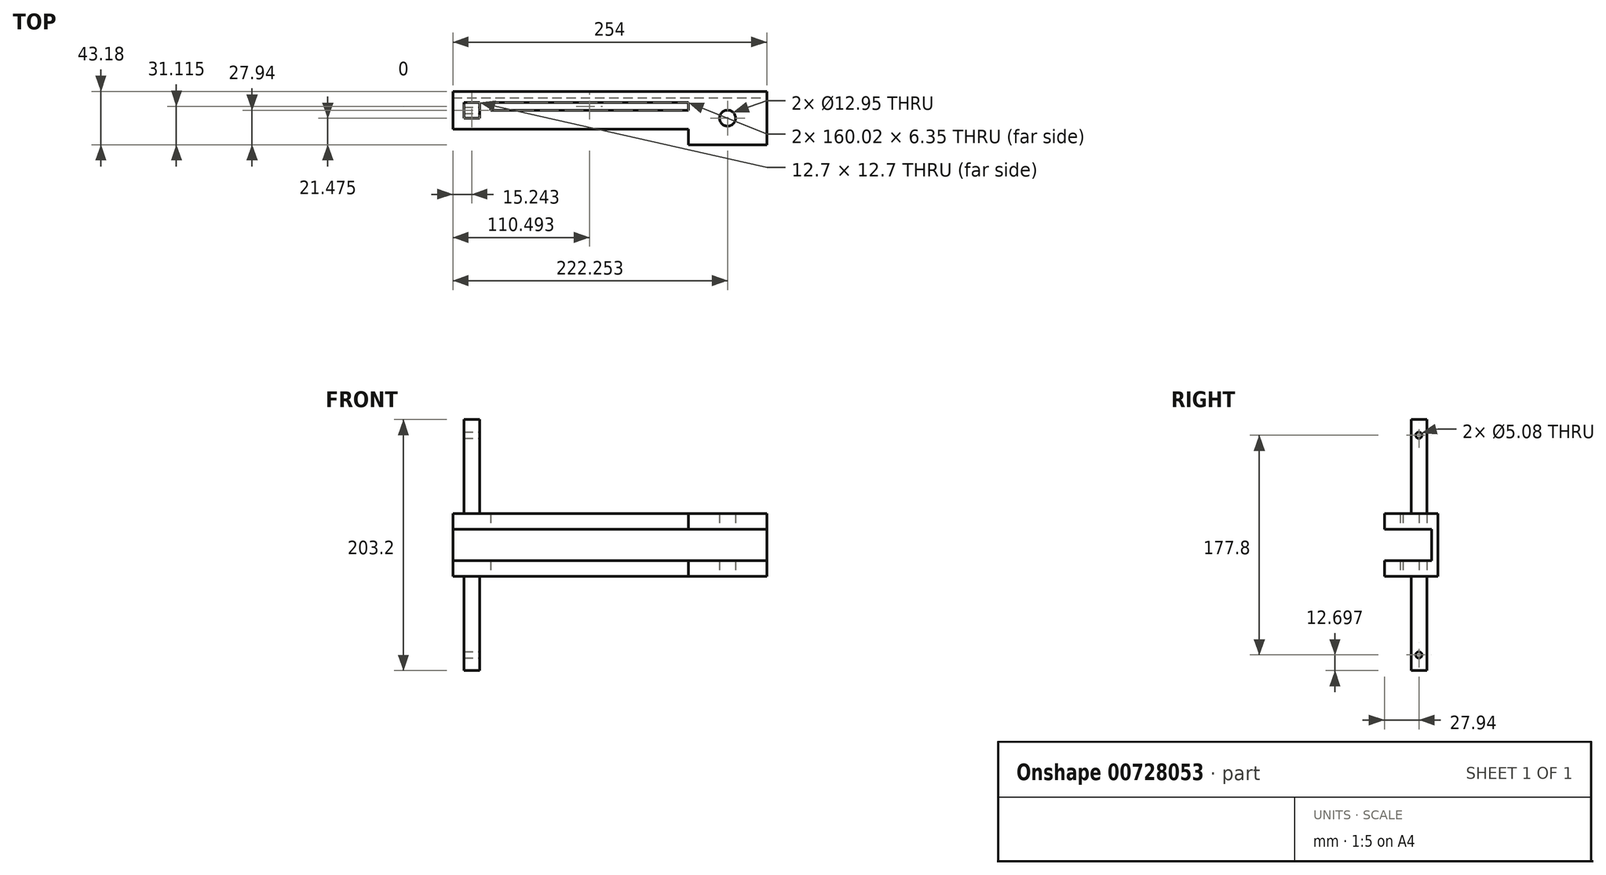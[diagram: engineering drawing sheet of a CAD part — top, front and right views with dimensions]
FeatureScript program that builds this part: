
annotation { "Feature Type Name" : "Feature", "Feature Type Description" : "" }
export const myFeature = defineFeature(function(context is Context, id is Id, definition is map)
    precondition{}
    {
        {
            var Q0;
            Q0=qCreatedBy(makeId("Front.planeOp"),FACE);
            var sketch = newSketch(context, id + "F0", { "sketchPlane" : qUnion([Q0])});
            skLineSegment(sketch, "E0.bottom", {"start": v(-131.64, 43.47) * mm, "end": v(122.36, 43.47) * mm});
            skLineSegment(sketch, "E0.top", {"start": v(-131.64, -7.33) * mm, "end": v(122.36, -7.33) * mm});
            skLineSegment(sketch, "E0.left", {"start": v(-131.64, 43.47) * mm, "end": v(-131.64, -7.33) * mm});
            skLineSegment(sketch, "E0.right", {"start": v(122.36, 43.47) * mm, "end": v(122.36, -7.33) * mm});
            skSolve(sketch);
        }
        {
            var Q0;
            Q0=makeQuery(id+"F0.imprint","IMPRINT",FACE,{"disambiguationData":[TD([[makeQuery(id+"F0.imprint","IMPRINT",EDGE,{"derivedFrom":sQuery(id+"F0.wireOp",EDGE,"E0.bottom")}),-1.0]])]});
            extrude(context, id + "F1", {"entities" : qUnion([Q0]), "depth" : 30.48 * mm, "offsetDistance" : 25.4 * mm});
        }
        {
            var Q0;
            Q0=makeQuery(id+"F1.opExtrude","CAP_FACE",FACE,{"disambiguationData":[OSD([sQuery(id+"F0.wireOp",EDGE,"E0.bottom"),sQuery(id+"F0.wireOp",EDGE,"E0.top"),sQuery(id+"F0.wireOp",EDGE,"E0.left"),sQuery(id+"F0.wireOp",EDGE,"E0.right")])],"isStart":false});
            var sketch = newSketch(context, id + "F2", { "sketchPlane" : qUnion([Q0])});
            skLineSegment(sketch, "E1", {"start": v(-131.64, 30.77) * mm, "end": v(122.36, 30.77) * mm});
            skLineSegment(sketch, "E2", {"start": v(-131.64, 5.37) * mm, "end": v(122.36, 5.37) * mm});
            skSolve(sketch);
        }
        {
            var Q0;
            {var subQ0=sQuery(id+"F2.wireOp",EDGE,"E1");Q0=makeQuery(id+"F2.imprint","IMPRINT",FACE,{"disambiguationData":[TD([[makeQuery(id+"F2.imprint","IMPRINT",EDGE,{"derivedFrom":subQ0}),-1.0]])]});}
            extrude(context, id + "F3", {"entities" : qUnion([Q0]), "operationType" : NewBodyOperationType.REMOVE, "oppositeDirection" : true, "depth" : 25.4 * mm, "offsetDistance" : 25.4 * mm});
        }
        {
            var Q0;
            Q0=makeQuery(id+"F1.opExtrude","SWEPT_FACE",FACE,{"disambiguationData":[OSD([sQuery(id+"F0.wireOp",EDGE,"E0.top")])]});
            var sketch = newSketch(context, id + "F4", { "sketchPlane" : qUnion([Q0])});
            skLineSegment(sketch, "E3.bottom", {"start": v(-122.75, 8.9) * mm, "end": v(-110.05, 8.9) * mm});
            skLineSegment(sketch, "E3.top", {"start": v(-122.75, 21.59) * mm, "end": v(-110.05, 21.59) * mm});
            skLineSegment(sketch, "E3.left", {"start": v(-122.75, 21.59) * mm, "end": v(-122.75, 8.89) * mm});
            skLineSegment(sketch, "E3.right", {"start": v(-110.05, 21.59) * mm, "end": v(-110.05, 8.89) * mm});
            skSolve(sketch);
        }
        {
            var Q0;
            Q0=makeQuery(id+"F1.opExtrude","SWEPT_FACE",FACE,{"disambiguationData":[OSD([sQuery(id+"F0.wireOp",EDGE,"E0.bottom")])]});
            var sketch = newSketch(context, id + "F5", { "sketchPlane" : qUnion([Q0])});
            skLineSegment(sketch, "E4.bottom", {"start": v(-110.05, -21.59) * mm, "end": v(-122.75, -21.59) * mm});
            skLineSegment(sketch, "E4.top", {"start": v(-110.05, -8.89) * mm, "end": v(-122.75, -8.89) * mm});
            skLineSegment(sketch, "E4.left", {"start": v(-110.05, -21.59) * mm, "end": v(-110.05, -8.89) * mm});
            skLineSegment(sketch, "E4.right", {"start": v(-122.75, -21.59) * mm, "end": v(-122.75, -8.89) * mm});
            skSolve(sketch);
        }
        {
            var Q0;
            Q0 = qSketchRegion(id + "F4", true);
            extrude(context, id + "F6", {"entities" : qUnion([Q0]), "operationType" : NewBodyOperationType.ADD, "depth" : 76.2 * mm, "offsetDistance" : 25.4 * mm});
        }
        {
            var Q0;
            Q0 = qSketchRegion(id + "F5", true);
            extrude(context, id + "F7", {"entities" : qUnion([Q0]), "operationType" : NewBodyOperationType.ADD, "depth" : 76.2 * mm, "offsetDistance" : 25.4 * mm});
        }
        {
            var Q0;
            {var subQ0=sQuery(id+"F0.wireOp",EDGE,"E0.bottom");var subQ1=sQuery(id+"F0.wireOp",EDGE,"E0.right");var subQ2=sQuery(id+"F0.wireOp",EDGE,"E0.left");Q0=makeQuery(id+"F3.boolean.opBoolean","SPLIT",FACE,{"disambiguationData":[TD([makeQuery(id+"F1.opExtrude","SWEPT_FACE",FACE,{"disambiguationData":[OSD([subQ0])]})])],"derivedFrom":makeQuery(id+"F1.opExtrude","CAP_FACE",FACE,{"disambiguationData":[OSD([subQ0,sQuery(id+"F0.wireOp",EDGE,"E0.top"),subQ2,subQ1])],"isStart":false})});}
            var sketch = newSketch(context, id + "F8", { "sketchPlane" : qUnion([Q0])});
            skLineSegment(sketch, "E5", {"start": v(58.86, 43.47) * mm, "end": v(58.86, 30.77) * mm});
            skSolve(sketch);
        }
        {
            var Q0;
            {var subQ0=sQuery(id+"F0.wireOp",EDGE,"E0.top");var subQ1=sQuery(id+"F0.wireOp",EDGE,"E0.left");var subQ2=sQuery(id+"F0.wireOp",EDGE,"E0.right");Q0=makeQuery(id+"F3.boolean.opBoolean","SPLIT",FACE,{"disambiguationData":[TD([makeQuery(id+"F1.opExtrude","SWEPT_FACE",FACE,{"disambiguationData":[OSD([subQ0])]})])],"derivedFrom":makeQuery(id+"F1.opExtrude","CAP_FACE",FACE,{"disambiguationData":[OSD([sQuery(id+"F0.wireOp",EDGE,"E0.bottom"),subQ0,subQ1,subQ2])],"isStart":false})});}
            var sketch = newSketch(context, id + "F9", { "sketchPlane" : qUnion([Q0])});
            skLineSegment(sketch, "E6", {"start": v(58.86, 5.37) * mm, "end": v(58.86, -7.33) * mm});
            skSolve(sketch);
        }
        {
            var Q0;
            {var subQ0=sQuery(id+"F8.wireOp",EDGE,"E5");Q0=makeQuery(id+"F8.imprint","IMPRINT",FACE,{"disambiguationData":[TD([[makeQuery(id+"F8.imprint","IMPRINT",EDGE,{"derivedFrom":subQ0}),1.0]])]});}
            extrude(context, id + "F10", {"entities" : qUnion([Q0]), "operationType" : NewBodyOperationType.ADD, "depth" : 12.7 * mm, "offsetDistance" : 25.4 * mm});
        }
        {
            var Q0;
            {var subQ0=sQuery(id+"F9.wireOp",EDGE,"E6");Q0=makeQuery(id+"F9.imprint","IMPRINT",FACE,{"disambiguationData":[TD([[makeQuery(id+"F9.imprint","IMPRINT",EDGE,{"derivedFrom":subQ0}),1.0]])]});}
            extrude(context, id + "F11", {"entities" : qUnion([Q0]), "operationType" : NewBodyOperationType.ADD, "depth" : 12.7 * mm, "offsetDistance" : 25.4 * mm});
        }
        {
            var Q0;
            Q0=makeQuery(id+"F4.imprint","IMPRINT",FACE,{"disambiguationData":[TD([[makeQuery(id+"F4.imprint","IMPRINT",EDGE,{"derivedFrom":sQuery(id+"F4.wireOp",EDGE,"E3.bottom")}),-1.0]])]});
            var sketch = newSketch(context, id + "F12", { "sketchPlane" : qUnion([Q0])});
            skLineSegment(sketch, "E7.bottom", {"start": v(-101.16, 15.24) * mm, "end": v(58.86, 15.24) * mm});
            skLineSegment(sketch, "E7.top", {"start": v(-101.16, 8.9) * mm, "end": v(58.86, 8.9) * mm});
            skLineSegment(sketch, "E7.left", {"start": v(-101.16, 15.24) * mm, "end": v(-101.16, 8.9) * mm});
            skLineSegment(sketch, "E7.right", {"start": v(58.86, 15.24) * mm, "end": v(58.86, 8.9) * mm});
            skSolve(sketch);
        }
        {
            var Q0;
            Q0=makeQuery(id+"F4.imprint","IMPRINT",FACE,{"disambiguationData":[TD([[makeQuery(id+"F4.imprint","IMPRINT",EDGE,{"derivedFrom":sQuery(id+"F4.wireOp",EDGE,"E3.bottom")}),-1.0]])]});
            var sketch = newSketch(context, id + "F13", { "sketchPlane" : qUnion([Q0])});
            skCircle(sketch, "E8", {"center": v(90.61, 21.7) * mm, "radius": 6.48 * mm});
            skSolve(sketch);
        }
        {
            var Q0;
            Q0=makeQuery(id+"F12.imprint","IMPRINT",FACE,{"disambiguationData":[TD([[makeQuery(id+"F12.imprint","IMPRINT",EDGE,{"derivedFrom":sQuery(id+"F12.wireOp",EDGE,"E7.bottom")}),-1.0]])]});
            extrude(context, id + "F14", {"entities" : qUnion([Q0]), "operationType" : NewBodyOperationType.REMOVE, "endBound" : BoundingType.THROUGH_ALL, "oppositeDirection" : true, "depth" : 25.4 * mm, "offsetDistance" : 25.4 * mm});
        }
        {
            var Q0;
            Q0 = qSketchRegion(id + "F13", true);
            extrude(context, id + "F15", {"entities" : qUnion([Q0]), "operationType" : NewBodyOperationType.REMOVE, "endBound" : BoundingType.THROUGH_ALL, "oppositeDirection" : true, "depth" : 25.4 * mm, "offsetDistance" : 25.4 * mm});
        }
        {
            var Q0;
            Q0=makeQuery(id+"F6.opExtrude","SWEPT_FACE",FACE,{"disambiguationData":[OSD([sQuery(id+"F4.wireOp",EDGE,"E3.right")])]});
            var sketch = newSketch(context, id + "F16", { "sketchPlane" : qUnion([Q0])});
            skCircle(sketch, "E9", {"center": v(-15.24, -70.83) * mm, "radius": 2.54 * mm});
            skSolve(sketch);
        }
        {
            var Q0;
            Q0=makeQuery(id+"F7.opExtrude","SWEPT_FACE",FACE,{"disambiguationData":[OSD([sQuery(id+"F5.wireOp",EDGE,"E4.left")])]});
            var sketch = newSketch(context, id + "F17", { "sketchPlane" : qUnion([Q0])});
            skCircle(sketch, "E10", {"center": v(-15.24, 106.97) * mm, "radius": 2.54 * mm});
            skSolve(sketch);
        }
        {
            var Q0;
            Q0=makeQuery(id+"F16.imprint","IMPRINT",FACE,{"disambiguationData":[TD([[makeQuery(id+"F16.imprint","IMPRINT",EDGE,{"derivedFrom":sQuery(id+"F16.wireOp",EDGE,"E9")}),1.0]])]});
            extrude(context, id + "F18", {"entities" : qUnion([Q0]), "operationType" : NewBodyOperationType.REMOVE, "oppositeDirection" : true, "depth" : 25.4 * mm, "offsetDistance" : 25.4 * mm});
        }
        {
            var Q0;
            Q0=makeQuery(id+"F17.imprint","IMPRINT",FACE,{"disambiguationData":[TD([[makeQuery(id+"F17.imprint","IMPRINT",EDGE,{"derivedFrom":sQuery(id+"F17.wireOp",EDGE,"E10")}),1.0]])]});
            extrude(context, id + "F19", {"entities" : qUnion([Q0]), "operationType" : NewBodyOperationType.REMOVE, "oppositeDirection" : true, "depth" : 25.4 * mm, "offsetDistance" : 25.4 * mm});
        }
    });
